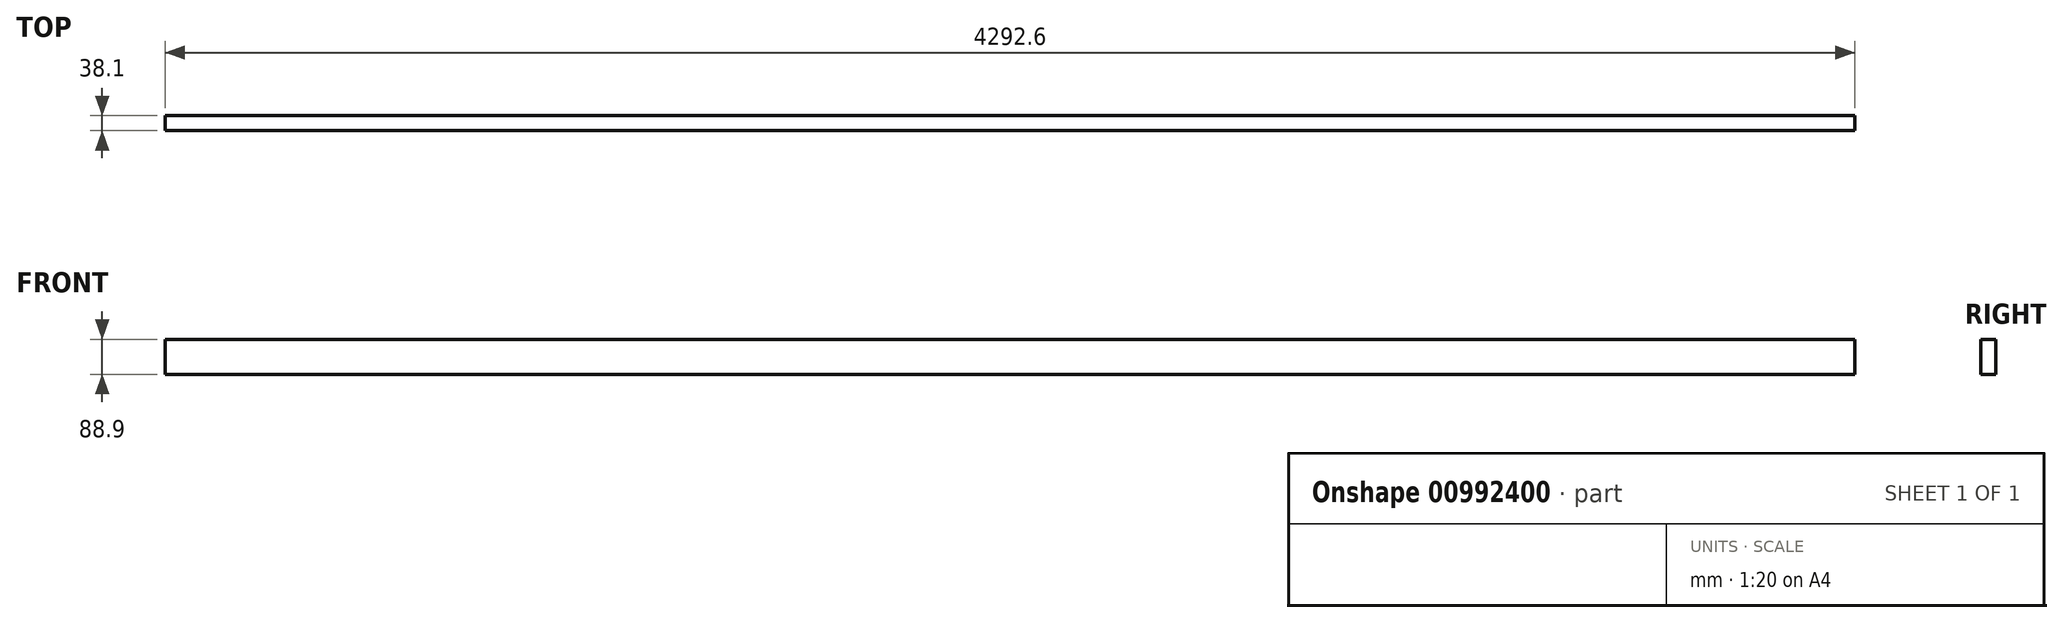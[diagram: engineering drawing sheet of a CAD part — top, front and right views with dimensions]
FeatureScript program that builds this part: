
annotation { "Feature Type Name" : "Feature", "Feature Type Description" : "" }
export const myFeature = defineFeature(function(context is Context, id is Id, definition is map)
    precondition{}
    {
        {
            var Q0;
            Q0=qCreatedBy(makeId("Front.planeOp"),FACE);
            var sketch = newSketch(context, id + "F0", { "sketchPlane" : qUnion([Q0])});
            skLineSegment(sketch, "E0.bottom", {"start": v(2146.3, 44.45) * mm, "end": v(-2146.3, 44.45) * mm});
            skLineSegment(sketch, "E0.top", {"start": v(2146.3, -44.45) * mm, "end": v(-2146.3, -44.45) * mm});
            skLineSegment(sketch, "E0.left", {"start": v(2146.3, 44.45) * mm, "end": v(2146.3, -44.45) * mm});
            skLineSegment(sketch, "E0.right", {"start": v(-2146.3, 44.45) * mm, "end": v(-2146.3, -44.45) * mm});
            skPoint(sketch, "E0.middle", {"position": v(0, 0) * mm});
            skSolve(sketch);
        }
        {
            var Q0;
            Q0=makeQuery(id+"F0.imprint","IMPRINT",FACE,{"disambiguationData":[TD([[makeQuery(id+"F0.imprint","IMPRINT",EDGE,{"derivedFrom":sQuery(id+"F0.wireOp",EDGE,"E0.bottom")}),1.0]])]});
            extrude(context, id + "F1", {"entities" : qUnion([Q0]), "depth" : 38.1 * mm, "offsetDistance" : 25.4 * mm});
        }
    });
